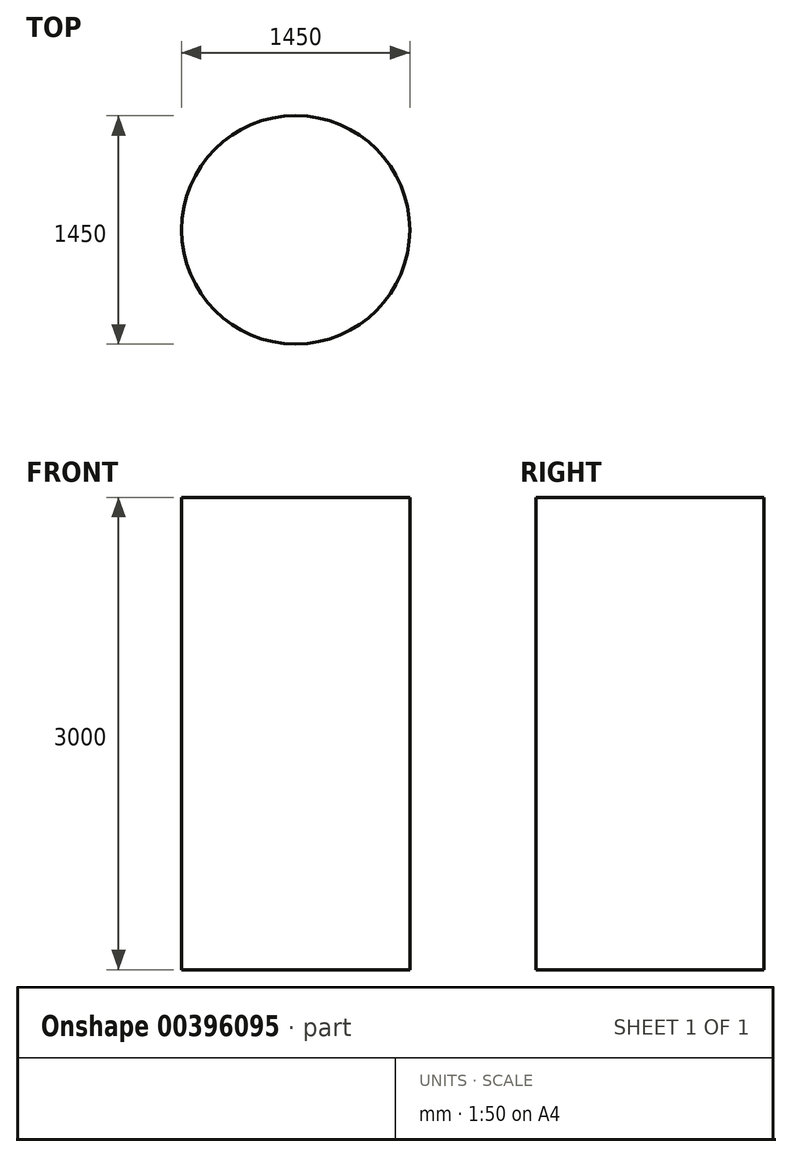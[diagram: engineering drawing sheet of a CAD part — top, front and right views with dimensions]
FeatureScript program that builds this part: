
annotation { "Feature Type Name" : "Feature", "Feature Type Description" : "" }
export const myFeature = defineFeature(function(context is Context, id is Id, definition is map)
    precondition{}
    {
        {
            var Q0;
            Q0=qCreatedBy(makeId("Top.planeOp"),FACE);
            var sketch = newSketch(context, id + "F0", { "sketchPlane" : qUnion([Q0])});
            skCircle(sketch, "E0", {"center": v(0, 0) * mm, "radius": 725 * mm});
            skSolve(sketch);
        }
        {
            var Q0;
            Q0=makeQuery(id+"F0.imprint","IMPRINT",FACE,{"disambiguationData":[TD([[makeQuery(id+"F0.imprint","IMPRINT",EDGE,{"derivedFrom":sQuery(id+"F0.wireOp",EDGE,"E0")}),1.0]])]});
            extrude(context, id + "F1", {"entities" : qUnion([Q0]), "depth" : 3000 * mm, "offsetDistance" : 25 * mm});
        }
    });
